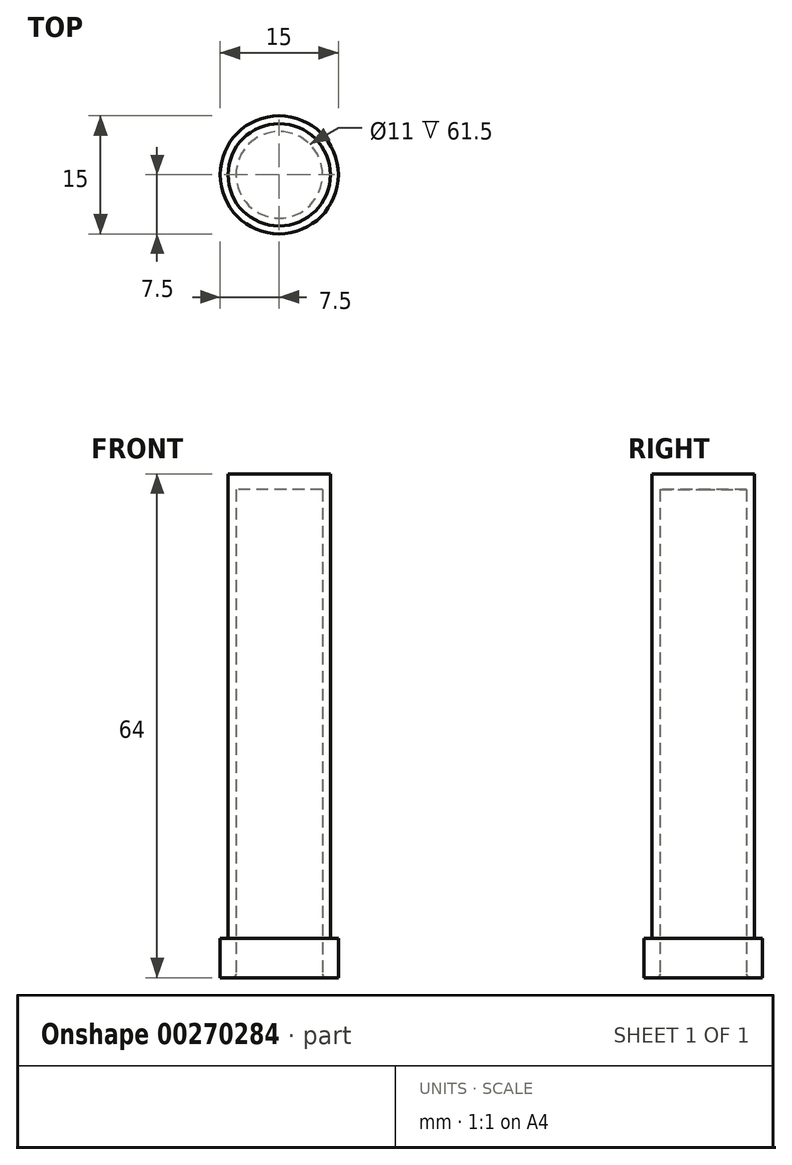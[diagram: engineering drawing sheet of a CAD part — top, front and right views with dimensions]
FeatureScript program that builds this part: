
annotation { "Feature Type Name" : "Feature", "Feature Type Description" : "" }
export const myFeature = defineFeature(function(context is Context, id is Id, definition is map)
    precondition{}
    {
        {
            var Q0;
            Q0=qCreatedBy(makeId("Top.planeOp"),FACE);
            var sketch = newSketch(context, id + "F0", { "sketchPlane" : qUnion([Q0])});
            skCircle(sketch, "E0", {"center": v(0, 0) * mm, "radius": 5.5 * mm});
            skCircle(sketch, "E1", {"center": v(0, 0) * mm, "radius": 6.5 * mm});
            skSolve(sketch);
        }
        {
            var Q0;
            Q0=makeQuery(id+"F0.imprint","IMPRINT",FACE,{"disambiguationData":[TD([[makeQuery(id+"F0.imprint","IMPRINT",EDGE,{"derivedFrom":sQuery(id+"F0.wireOp",EDGE,"E0")}),-1.0]])]});
            extrude(context, id + "F1", {"entities" : qUnion([Q0]), "depth" : 62 * mm});
        }
        {
            var Q0;
            Q0=makeQuery(id+"F1.opExtrude","CAP_FACE",FACE,{"disambiguationData":[OSD([sQuery(id+"F0.wireOp",EDGE,"E0"),sQuery(id+"F0.wireOp",EDGE,"E1")])],"isStart":false});
            var sketch = newSketch(context, id + "F2", { "sketchPlane" : qUnion([Q0])});
            skCircle(sketch, "E2", {"center": v(0, 0) * mm, "radius": 6.5 * mm});
            skSolve(sketch);
        }
        {
            var Q0;
            Q0 = qSketchRegion(id + "F2", true);
            extrude(context, id + "F3", {"entities" : qUnion([Q0]), "operationType" : NewBodyOperationType.ADD, "depth" : 2 * mm});
        }
        {
            var Q0;
            Q0=qCreatedBy(makeId("Top.planeOp"),FACE);
            var sketch = newSketch(context, id + "F4", { "sketchPlane" : qUnion([Q0])});
            skCircle(sketch, "E3", {"center": v(0, 0) * mm, "radius": 7.5 * mm});
            skCircle(sketch, "E4", {"center": v(0, 0) * mm, "radius": 6.5 * mm});
            skSolve(sketch);
        }
        {
            var Q0;
            Q0 = qSketchRegion(id + "F4", true);
            extrude(context, id + "F5", {"entities" : qUnion([Q0]), "operationType" : NewBodyOperationType.ADD, "depth" : 5 * mm});
        }
        {
            var Q0;
            Q0=makeQuery(id+"F1.opExtrude","CAP_EDGE",EDGE,{"disambiguationData":[OSD([sQuery(id+"F0.wireOp",EDGE,"E0")])],"isStart":true});
            fillet(context, id + "F6", {"entities" : qUnion([Q0]), "radius" : .5 * mm, "tangentPropagation" : true, "allowEdgeOverflow" : false});
        }
    });
